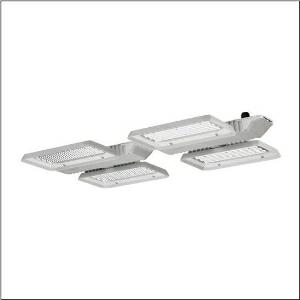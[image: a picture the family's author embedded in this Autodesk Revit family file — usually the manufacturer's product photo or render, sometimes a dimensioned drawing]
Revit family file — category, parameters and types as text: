
# Revit family: highbay_21_51hlasd24mgb
name_source: partatom
category: Lighting Fixtures
units: mm (PartAtom-declared; Revit-internal decimal feet)

## family parameters
Cut with Voids When Loaded = No
Host = Face
Light Source = No
Part Type = Normal
Room Calculation Point = No
Round Connector Dimension = Use Diameter
Shared = No

## types (1)
- --- (1 x LED, 27600 lm, 171.1 W, 4000K)
    Apparent Load = 171 VA
    CIE Flux Codes = 89 96 99 100 100
    Color Rendering = 80
    Color Temperature = 4000K
    Default Elevation = 1800 mm
    Description = Highbay 21, LED high bay luminaire, primary light control with lens, of PMMA, light emission: direct distribution, primary light characteristic: symmetric, installation type: suspended mounting, for 2x 2 x LED rated luminous flux: 27.600 lm, light colour: 840, colour temperature: 4000K, control gear: ECG DALI, with terminal, 5-pole, max. 2.5mm², mains connection: 230..240V, AC, 50/60Hz, rated input power: 171W, LED unit, of diecast aluminium, unplated, bead blasted, silver, length: 940 mm, width: 500 mm, height: 65mm, housing, of diecast aluminium, uncoated, bead blasted, silver, protection rating (complete): IP20, insulation class (complete): insulation class I (protective earthing), certification: CE, ENEC, VDE, protection symbol: D, ball protection: ball impact resistant according to DIN VDE 0710 part 13 (with chain suspension), permissible ambient temperature for indoor applications: -35..+45°C, corresponds to IFS (International Featured Standards) requirements for safety and quality in the food industry, reducing of maximum allowable ambient temperature of 5°C with ceiling mounting, packaging unit: 1 piece
    Height = 95 mm
    Lamp = 1 x LED
    Lamp Light Flux = 27600 lm
    Lamp Power = 171.1 W
    Lamp count = 1
    Length = 939 mm
    Luminous efficacy = 161 lm/W
    Manufacturer = Siteco
    ModVariant = No
    Model = 51HLASD24MGB
    Mounting Place = Ceiling
    Mounting Type = Pendant
    Number of Poles = 1
    OnlyDefault = Yes
    Power Factor = 1
    Product Name = Highbay 21
    Product group = LED high bay luminaire
    ProductGroupID = 903
    Protection Class = Protection class I
    Protection Degree = IP 20
    RLX_Detail_Level = 1
    RlxData = <blob elided: 64701 chars, md5=1dee3af0>
    Socket = socket
    Standby Power = 0 W
    System Light Flux = 27600 lm
    System Power = 171 W
    Type Comments = factory setting: luminous flux: 100 % | dim-lin: 254 | 491 mA
    Type Image = l_1006021.jpg
    URL = http://relux.com
    VarID = @adj_135603
    Voltage = 0 V
    Weight = 0.00 kg
    Width = 501 mm

## geometry (parser evidence)
native form markers: Blend x4, Sweep x11
no freeform markers — native parametric forms only
